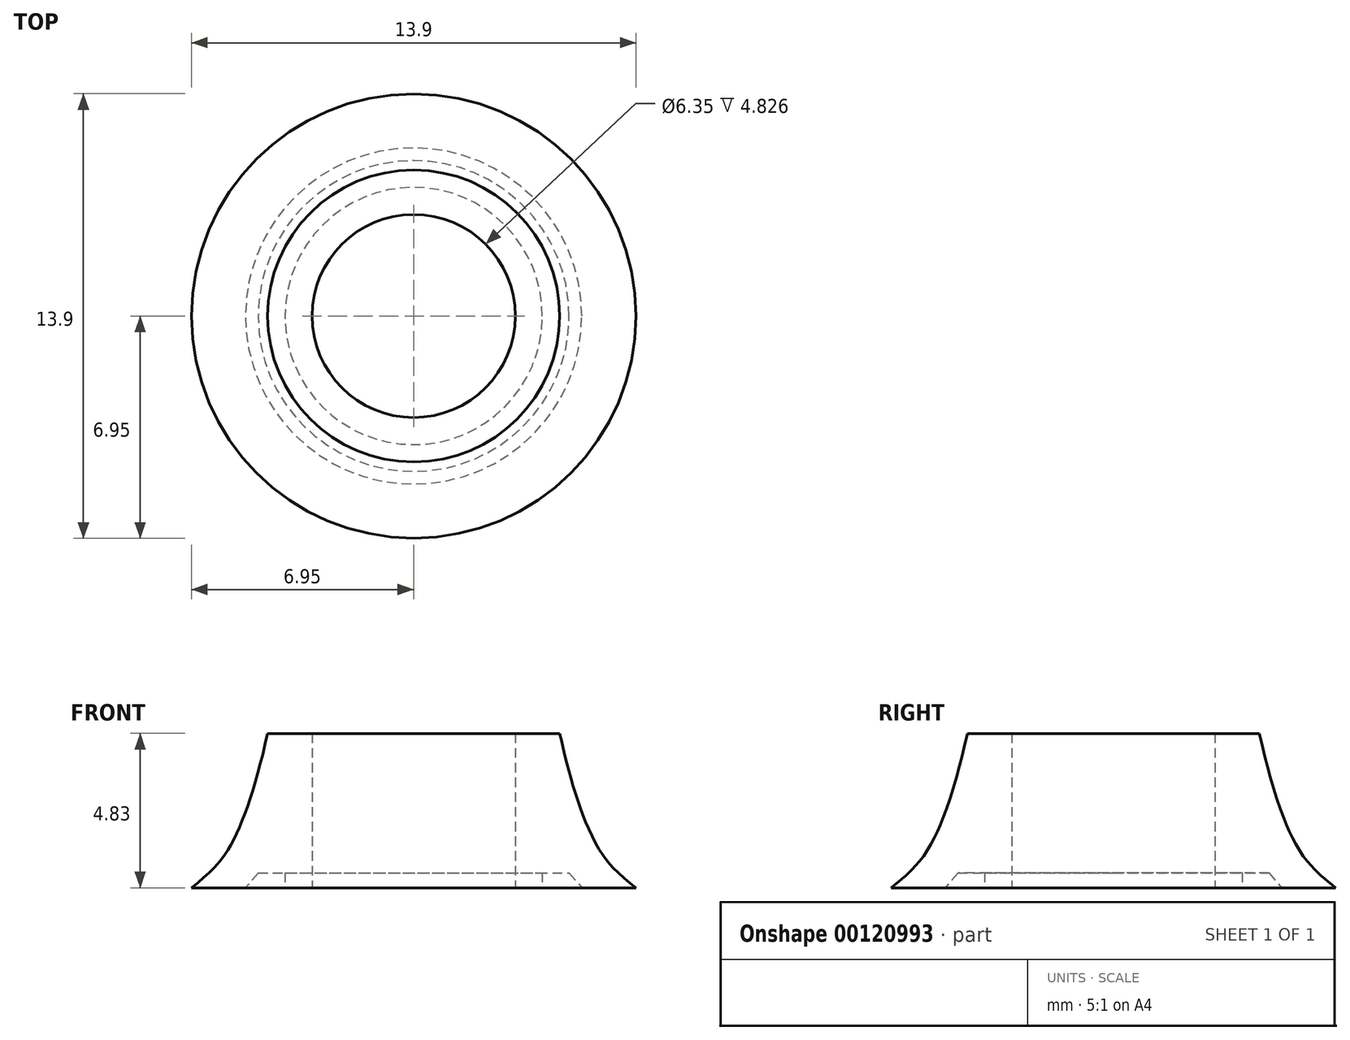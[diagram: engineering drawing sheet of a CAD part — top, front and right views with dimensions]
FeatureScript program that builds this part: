
annotation { "Feature Type Name" : "Feature", "Feature Type Description" : "" }
export const myFeature = defineFeature(function(context is Context, id is Id, definition is map)
    precondition{}
    {
        {
            var Q0;
            Q0=qCreatedBy(makeId("Front.planeOp"),FACE);
            var sketch = newSketch(context, id + "F0", { "sketchPlane" : qUnion([Q0])});
            skLineSegment(sketch, "E0", {"start": v(0, 0) * mm, "end": v(0, 8.44) * mm});
            skLineSegment(sketch, "E1", {"start": v(-3.18, 4.83) * mm, "end": v(-4.57, 4.83) * mm});
            skLineSegment(sketch, "E2", {"start": v(-6.95, 0) * mm, "end": v(-5.26, 0) * mm});
            skLineSegment(sketch, "E3", {"start": v(-5.26, 0) * mm, "end": v(-4.86, 0.47) * mm});
            skLineSegment(sketch, "E4", {"start": v(-4.86, 0.47) * mm, "end": v(-4.02, 0.47) * mm});
            skLineSegment(sketch, "E5", {"start": v(-4.02, 0.47) * mm, "end": v(-4.02, 0) * mm});
            skLineSegment(sketch, "E6", {"start": v(-4.02, 0) * mm, "end": v(-3.17, 0) * mm});
            skLineSegment(sketch, "E7", {"start": v(-3.17, 0) * mm, "end": v(-3.18, 4.83) * mm});
            skFitSpline(sketch, "E8", {"points": [v(-4.57, 4.83) * mm, v(-5.64, 1.49) * mm, v(-6.95, 0) * mm], "startDerivative": vector(-1.7, -7.66) * mm, "endDerivative": vector(-5, -3.95) * mm});
            skSolve(sketch);
        }
        {
            var Q0;
            Q0=qSketchRegion(id+"F0",true);
            var Q1;
            Q1=sQuery(id+"F0.wireOp",EDGE,"E0");
            revolve(context, id + "F1", {"entities" : qUnion([Q0]), "axis" : qUnion([Q1]), "revolveType" : RevolveType.FULL});
        }
    });
